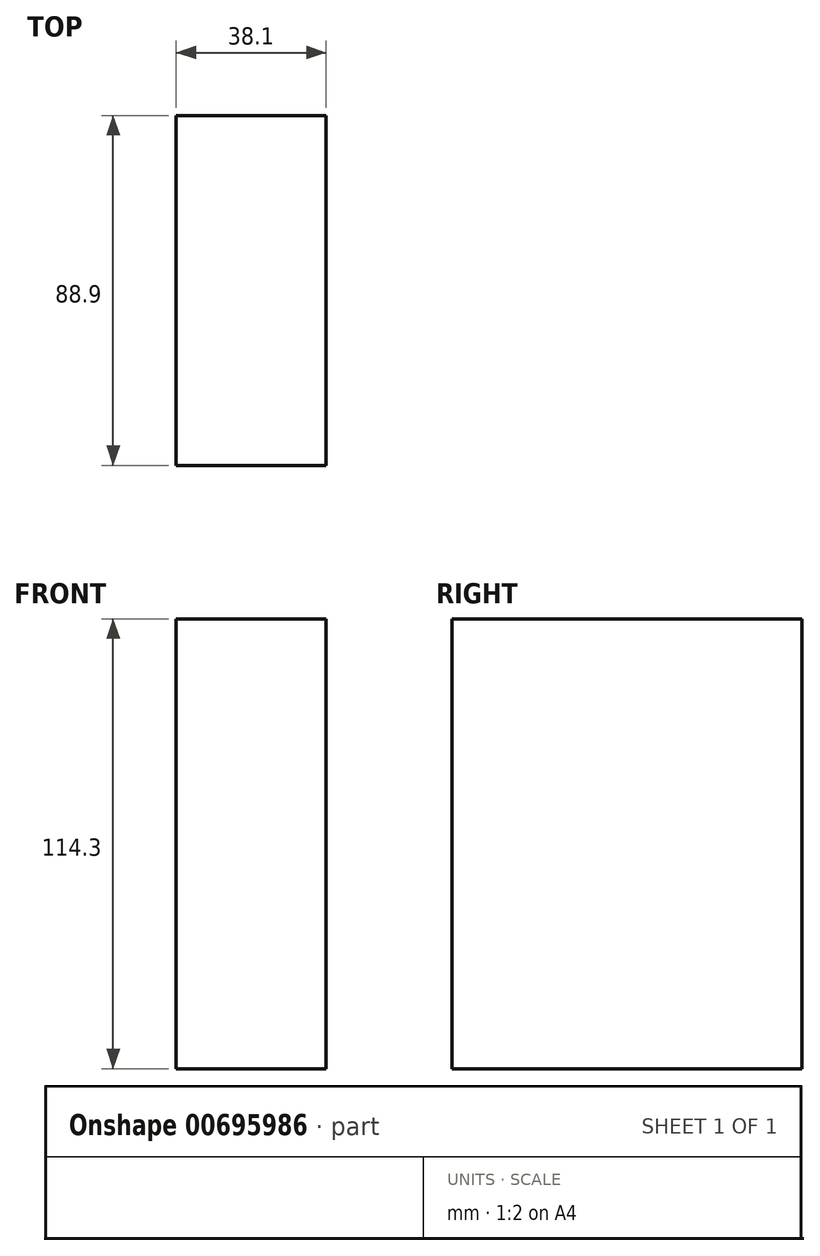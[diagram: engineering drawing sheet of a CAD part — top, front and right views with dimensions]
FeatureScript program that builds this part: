
annotation { "Feature Type Name" : "Feature", "Feature Type Description" : "" }
export const myFeature = defineFeature(function(context is Context, id is Id, definition is map)
    precondition{}
    {
        {
            var Q0;
            Q0=qCreatedBy(makeId("Right.planeOp"),FACE);
            var sketch = newSketch(context, id + "F0", { "sketchPlane" : qUnion([Q0])});
            skLineSegment(sketch, "E0.bottom", {"start": v(0, 0) * mm, "end": v(-88.9, 0) * mm});
            skLineSegment(sketch, "E0.top", {"start": v(0, 114.3) * mm, "end": v(-88.9, 114.3) * mm});
            skLineSegment(sketch, "E0.left", {"start": v(0, 0) * mm, "end": v(0, 114.3) * mm});
            skLineSegment(sketch, "E0.right", {"start": v(-88.9, 0) * mm, "end": v(-88.9, 114.3) * mm});
            skSolve(sketch);
        }
        {
            var Q0;
            Q0 = qSketchRegion(id + "F0", true);
            extrude(context, id + "F1", {"entities" : qUnion([Q0]), "depth" : 38.1 * mm, "offsetDistance" : 25.4 * mm});
        }
    });
